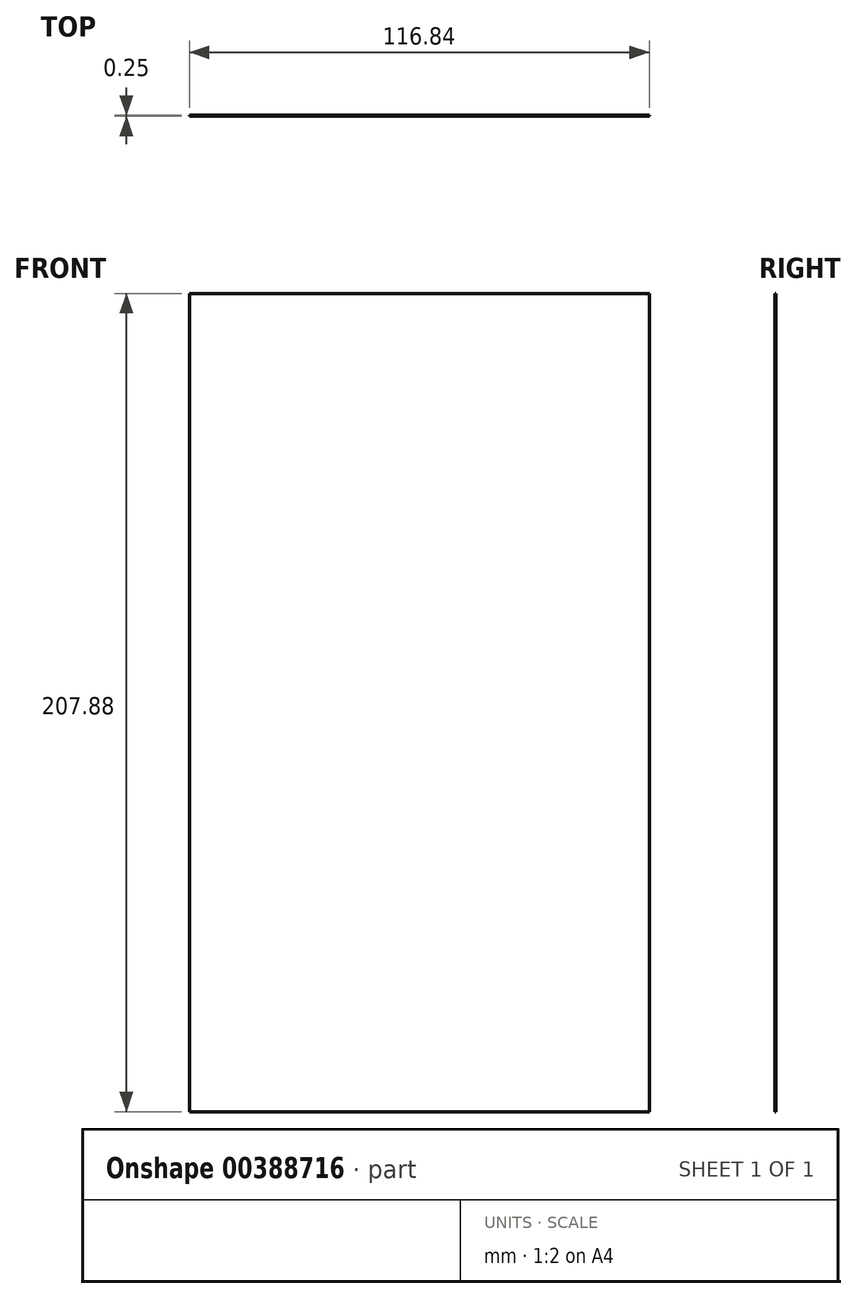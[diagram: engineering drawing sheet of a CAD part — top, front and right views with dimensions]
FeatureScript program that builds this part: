
annotation { "Feature Type Name" : "Feature", "Feature Type Description" : "" }
export const myFeature = defineFeature(function(context is Context, id is Id, definition is map)
    precondition{}
    {
        {
            var Q0;
            Q0=qCreatedBy(makeId("Front.planeOp"),FACE);
            var sketch = newSketch(context, id + "F0", { "sketchPlane" : qUnion([Q0])});
            skLineSegment(sketch, "E0.bottom", {"start": v(-58.42, -103.94) * mm, "end": v(58.42, -103.94) * mm});
            skLineSegment(sketch, "E0.top", {"start": v(-58.42, 103.94) * mm, "end": v(58.42, 103.94) * mm});
            skLineSegment(sketch, "E0.left", {"start": v(-58.42, -103.94) * mm, "end": v(-58.42, 103.94) * mm});
            skLineSegment(sketch, "E0.right", {"start": v(58.42, -103.94) * mm, "end": v(58.42, 103.94) * mm});
            skSolve(sketch);
        }
        {
            var Q0;
            Q0 = qSketchRegion(id + "F0", true);
            extrude(context, id + "F1", {"entities" : qUnion([Q0]), "depth" : 0.25 * mm});
        }
    });
